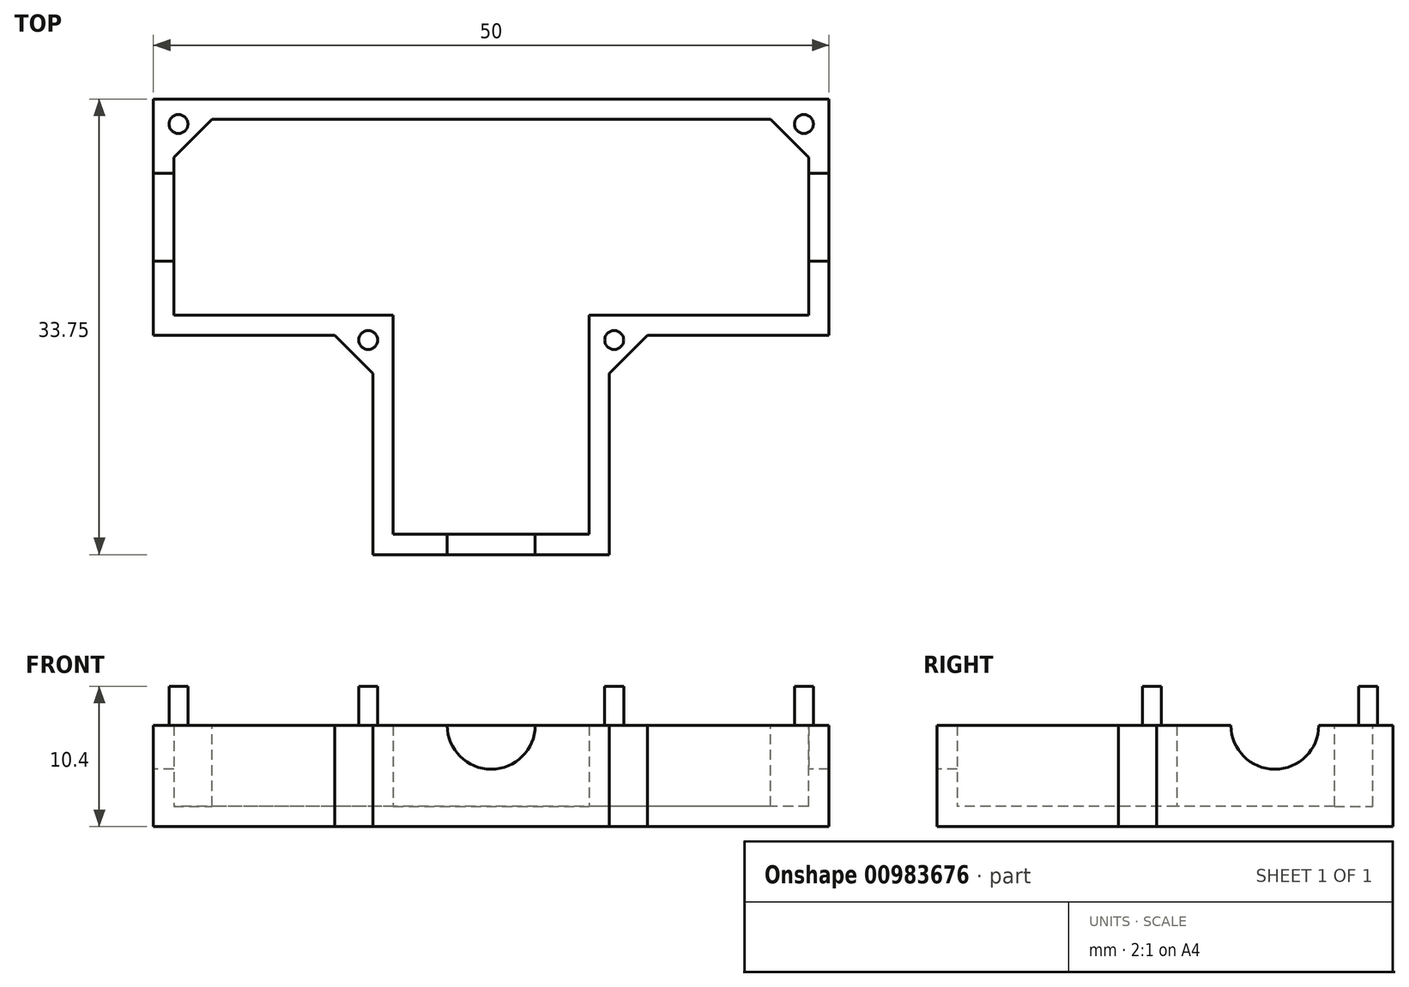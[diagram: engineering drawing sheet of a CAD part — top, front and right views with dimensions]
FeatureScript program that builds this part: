
annotation { "Feature Type Name" : "Feature", "Feature Type Description" : "" }
export const myFeature = defineFeature(function(context is Context, id is Id, definition is map)
    precondition{}
    {
        {
            var Q0;
            Q0=qCreatedBy(makeId("Top.planeOp"),FACE);
            var sketch = newSketch(context, id + "F0", { "sketchPlane" : qUnion([Q0])});
            skLineSegment(sketch, "E0.bottom", {"start": v(25, 8.75) * mm, "end": v(8.75, 8.75) * mm});
            skLineSegment(sketch, "E0.top", {"start": v(25, -8.75) * mm, "end": v(8.75, -8.75) * mm});
            skLineSegment(sketch, "E0.left", {"start": v(25, 8.75) * mm, "end": v(25, -8.75) * mm});
            skLineSegment(sketch, "E0.right", {"start": v(-25, 8.75) * mm, "end": v(-25, -8.75) * mm});
            skPoint(sketch, "E0.middle", {"position": v(0, 0) * mm});
            skLineSegment(sketch, "E1.top", {"start": v(-8.75, -25) * mm, "end": v(8.75, -25) * mm});
            skLineSegment(sketch, "E2.trimOffspring", {"start": v(-8.75, 8.75) * mm, "end": v(-25, 8.75) * mm});
            skLineSegment(sketch, "E3.trimOffspring", {"start": v(-8.75, -8.75) * mm, "end": v(-8.75, -25) * mm});
            skLineSegment(sketch, "E4.trimOffspring", {"start": v(-8.75, -8.75) * mm, "end": v(-25, -8.75) * mm});
            skLineSegment(sketch, "E5.trimOffspring", {"start": v(8.75, -8.75) * mm, "end": v(8.75, -25) * mm});
            skLineSegment(sketch, "E6", {"start": v(8.75, 8.75) * mm, "end": v(-8.75, 8.75) * mm});
            skLineSegment(sketch, "E7", {"start": v(0, 0) * mm, "end": v(0, -25) * mm});
            skSolve(sketch);
        }
        {
            var Q0;
            Q0=qSketchRegion(id+"F0",true);
            extrude(context, id + "F1", {"entities" : qUnion([Q0]), "depth" : 7.5 * mm, "offsetDistance" : 25 * mm});
        }
        {
            var Q0;
            Q0=makeQuery(id+"F1.opExtrude","CAP_FACE",FACE,{"disambiguationData":[OSD([sQuery(id+"F0.wireOp",EDGE,"E0.bottom"),sQuery(id+"F0.wireOp",EDGE,"E0.top"),sQuery(id+"F0.wireOp",EDGE,"E0.left"),sQuery(id+"F0.wireOp",EDGE,"E0.right"),sQuery(id+"F0.wireOp",EDGE,"E1.bottom"),sQuery(id+"F0.wireOp",EDGE,"E1.top"),sQuery(id+"F0.wireOp",EDGE,"E1.left"),sQuery(id+"F0.wireOp",EDGE,"E1.right"),sQuery(id+"F0.wireOp",EDGE,"E2.trimOffspring"),sQuery(id+"F0.wireOp",EDGE,"E3.trimOffspring"),sQuery(id+"F0.wireOp",EDGE,"E4.trimOffspring"),sQuery(id+"F0.wireOp",EDGE,"E5.trimOffspring")])],"isStart":false});
            shell(context, id + "F2", {"entities" : qUnion([Q0]), "thickness" : 1.5 * mm});
        }
        {
            var Q0;
            Q0=makeQuery(id+"F1.opExtrude","CAP_FACE",FACE,{"disambiguationData":[OSD([sQuery(id+"F0.wireOp",EDGE,"E0.bottom"),sQuery(id+"F0.wireOp",EDGE,"E0.top"),sQuery(id+"F0.wireOp",EDGE,"E0.left"),sQuery(id+"F0.wireOp",EDGE,"E0.right"),sQuery(id+"F0.wireOp",EDGE,"E1.top"),sQuery(id+"F0.wireOp",EDGE,"E2.trimOffspring"),sQuery(id+"F0.wireOp",EDGE,"E3.trimOffspring"),sQuery(id+"F0.wireOp",EDGE,"E4.trimOffspring"),sQuery(id+"F0.wireOp",EDGE,"E5.trimOffspring"),sQuery(id+"F0.wireOp",EDGE,"E6")])],"isStart":false});
            var sketch = newSketch(context, id + "F3", { "sketchPlane" : qUnion([Q0])});
            skLineSegment(sketch, "E8", {"start": v(-23.5, 4.42) * mm, "end": v(-20.67, 7.25) * mm});
            skLineSegment(sketch, "E9", {"start": v(-20.67, 7.25) * mm, "end": v(-23.5, 7.25) * mm});
            skLineSegment(sketch, "E10", {"start": v(-23.5, 7.25) * mm, "end": v(-23.5, 4.42) * mm});
            skLineSegment(sketch, "E11", {"start": v(0, 7.25) * mm, "end": v(0, 0) * mm});
            skLineSegment(sketch, "E12", {"start": v(-11.58, -8.75) * mm, "end": v(-8.75, -8.75) * mm});
            skLineSegment(sketch, "E13", {"start": v(-8.75, -8.75) * mm, "end": v(-8.75, -11.58) * mm});
            skLineSegment(sketch, "E14", {"start": v(-8.75, -11.58) * mm, "end": v(-11.58, -8.75) * mm});
            skLineSegment(sketch, "E15.MirrorCS", {"start": v(20.67, 7.25) * mm, "end": v(23.5, 7.25) * mm});
            skLineSegment(sketch, "E16.MirrorCS", {"start": v(11.58, -8.75) * mm, "end": v(8.75, -8.75) * mm});
            skLineSegment(sketch, "E17.MirrorCS", {"start": v(23.5, 4.42) * mm, "end": v(20.67, 7.25) * mm});
            skLineSegment(sketch, "E18.MirrorCS", {"start": v(8.75, -11.58) * mm, "end": v(11.58, -8.75) * mm});
            skLineSegment(sketch, "E19.MirrorCS", {"start": v(23.5, 7.25) * mm, "end": v(23.5, 4.42) * mm});
            skLineSegment(sketch, "E20.MirrorCS", {"start": v(8.75, -8.75) * mm, "end": v(8.75, -11.58) * mm});
            skSolve(sketch);
        }
        {
            var Q0;
            Q0=qSketchRegion(id+"F3",true);
            var Q1;
            Q1=makeQuery(id+"F1.opExtrude","CAP_FACE",FACE,{"disambiguationData":[OSD([sQuery(id+"F0.wireOp",EDGE,"E0.bottom"),sQuery(id+"F0.wireOp",EDGE,"E0.top"),sQuery(id+"F0.wireOp",EDGE,"E0.left"),sQuery(id+"F0.wireOp",EDGE,"E0.right"),sQuery(id+"F0.wireOp",EDGE,"E1.top"),sQuery(id+"F0.wireOp",EDGE,"E2.trimOffspring"),sQuery(id+"F0.wireOp",EDGE,"E3.trimOffspring"),sQuery(id+"F0.wireOp",EDGE,"E4.trimOffspring"),sQuery(id+"F0.wireOp",EDGE,"E5.trimOffspring"),sQuery(id+"F0.wireOp",EDGE,"E6")])],"isStart":true});
            extrude(context, id + "F4", {"entities" : qUnion([Q0]), "operationType" : NewBodyOperationType.ADD, "endBound" : BoundingType.UP_TO_SURFACE, "oppositeDirection" : true, "depth" : 25 * mm, "endBoundEntityFace" : qUnion([Q1]), "offsetDistance" : 25 * mm});
        }
        {
            var Q0;
            Q0=makeQuery(id+"F4.boolean.opBoolean","MERGE",FACE,{"derivedFrom":[makeQuery(id+"F1.opExtrude","CAP_FACE",FACE,{"disambiguationData":[OSD([sQuery(id+"F0.wireOp",EDGE,"E0.bottom"),sQuery(id+"F0.wireOp",EDGE,"E0.top"),sQuery(id+"F0.wireOp",EDGE,"E0.left"),sQuery(id+"F0.wireOp",EDGE,"E0.right"),sQuery(id+"F0.wireOp",EDGE,"E1.top"),sQuery(id+"F0.wireOp",EDGE,"E2.trimOffspring"),sQuery(id+"F0.wireOp",EDGE,"E3.trimOffspring"),sQuery(id+"F0.wireOp",EDGE,"E4.trimOffspring"),sQuery(id+"F0.wireOp",EDGE,"E5.trimOffspring"),sQuery(id+"F0.wireOp",EDGE,"E6")])],"isStart":false}),makeQuery(id+"F4.opExtrude","CAP_FACE",FACE,{"disambiguationData":[OSD([sQuery(id+"F3.wireOp",EDGE,"E8"),sQuery(id+"F3.wireOp",EDGE,"E9"),sQuery(id+"F3.wireOp",EDGE,"E10")])],"isStart":true}),makeQuery(id+"F4.opExtrude","CAP_FACE",FACE,{"disambiguationData":[OSD([sQuery(id+"F3.wireOp",EDGE,"E12"),sQuery(id+"F3.wireOp",EDGE,"E13"),sQuery(id+"F3.wireOp",EDGE,"E14")])],"isStart":true}),makeQuery(id+"F4.opExtrude","CAP_FACE",FACE,{"disambiguationData":[OSD([sQuery(id+"F3.wireOp",EDGE,"E15.MirrorCS"),sQuery(id+"F3.wireOp",EDGE,"E17.MirrorCS"),sQuery(id+"F3.wireOp",EDGE,"E19.MirrorCS")])],"isStart":true}),makeQuery(id+"F4.opExtrude","CAP_FACE",FACE,{"disambiguationData":[OSD([sQuery(id+"F3.wireOp",EDGE,"E16.MirrorCS"),sQuery(id+"F3.wireOp",EDGE,"E18.MirrorCS"),sQuery(id+"F3.wireOp",EDGE,"E20.MirrorCS")])],"isStart":true})]});
            var sketch = newSketch(context, id + "F5", { "sketchPlane" : qUnion([Q0])});
            skCircle(sketch, "E21", {"center": v(-9.1, -9.1) * mm, "radius": 0.7 * mm});
            skCircle(sketch, "E22", {"center": v(-23.15, 6.9) * mm, "radius": 0.7 * mm});
            skCircle(sketch, "E23", {"center": v(9.1, -9.1) * mm, "radius": 0.7 * mm});
            skCircle(sketch, "E24", {"center": v(23.15, 6.9) * mm, "radius": 0.7 * mm});
            skLineSegment(sketch, "E25", {"start": v(-9.1, -9.1) * mm, "end": v(-10.16, -10.16) * mm});
            skLineSegment(sketch, "E26", {"start": v(9.1, -9.1) * mm, "end": v(10.16, -10.16) * mm});
            skLineSegment(sketch, "E27", {"start": v(23.15, 6.9) * mm, "end": v(22.09, 5.84) * mm});
            skLineSegment(sketch, "E28", {"start": v(-23.15, 6.9) * mm, "end": v(-22.09, 5.84) * mm});
            skSolve(sketch);
        }
        {
            var Q0;
            Q0=qSketchRegion(id+"F5",true);
            extrude(context, id + "F6", {"entities" : qUnion([Q0]), "operationType" : NewBodyOperationType.ADD, "depth" : 2.9 * mm, "offsetDistance" : 25 * mm});
        }
        {
            var Q0;
            Q0=makeQuery(id+"F1.opExtrude","SWEPT_FACE",FACE,{"disambiguationData":[OSD([sQuery(id+"F0.wireOp",EDGE,"E1.top")])]});
            var sketch = newSketch(context, id + "F7", { "sketchPlane" : qUnion([Q0])});
            skCircle(sketch, "E29", {"center": v(0, 7.5) * mm, "radius": 3.25 * mm});
            skSolve(sketch);
        }
        {
            var Q0;
            Q0=qSketchRegion(id+"F7",true);
            var Q1;
            Q1=makeQuery(id+"F2.opShell","OFFSET_FACE",FACE,{"disambiguationData":[OSD([sQuery(id+"F0.wireOp",EDGE,"E0.bottom"),sQuery(id+"F0.wireOp",EDGE,"E2.trimOffspring"),sQuery(id+"F0.wireOp",EDGE,"E6")])]});
            extrude(context, id + "F8", {"entities" : qUnion([Q0]), "operationType" : NewBodyOperationType.REMOVE, "endBound" : BoundingType.UP_TO_SURFACE, "oppositeDirection" : true, "depth" : 25 * mm, "endBoundEntityFace" : qUnion([Q1]), "offsetDistance" : 25 * mm});
        }
        {
            var Q0;
            Q0=makeQuery(id+"F1.opExtrude","SWEPT_FACE",FACE,{"disambiguationData":[OSD([sQuery(id+"F0.wireOp",EDGE,"E0.right")])]});
            var sketch = newSketch(context, id + "F9", { "sketchPlane" : qUnion([Q0])});
            skCircle(sketch, "E30", {"center": v(0, 7.5) * mm, "radius": 3.25 * mm});
            skSolve(sketch);
        }
        {
            var Q0;
            Q0=qSketchRegion(id+"F9",true);
            extrude(context, id + "F10", {"entities" : qUnion([Q0]), "operationType" : NewBodyOperationType.REMOVE, "endBound" : BoundingType.THROUGH_ALL, "oppositeDirection" : true, "depth" : 25 * mm, "offsetDistance" : 25 * mm});
        }
    });
